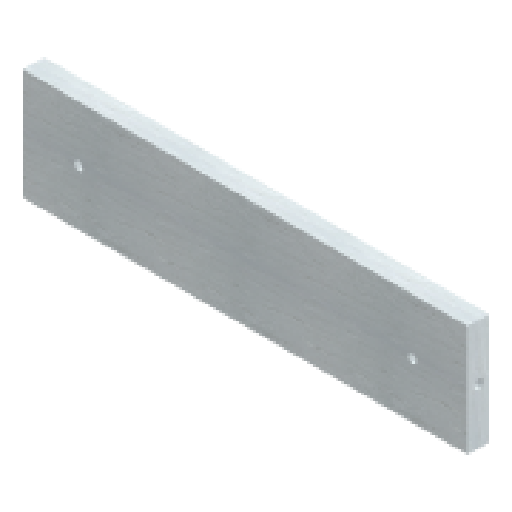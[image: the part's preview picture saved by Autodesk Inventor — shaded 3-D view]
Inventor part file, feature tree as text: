
AUTODESK INVENTOR PART (.ipt)
format: ipt  version: 2024 (Build 280153000, 153)  size: 125,440 bytes
history: native  units: in
note: dims shown in document units (in); Inventor stores cm internally (conversion verified against a paired STEP export)
features: extrude x4, sketch x4
ambient origin geometry x8: Origin, YZ Plane, XZ Plane, XY Plane, X Axis, Y Axis, Z Axis, Center Point
bodies: Solid1 (feature_tree)
feature tree (8):
  extrude  "Extrusion1"  Depth=3.937in
  extrude  "Extrusion2"  Depth=0.374in
  extrude  "Extrusion3"  Depth=0.315in
  extrude  "Extrusion4"  Depth=0.4331in TaperAngle=0.0deg
  sketch  "Sketch1"  dims[d0=15.748in d1=3.937in]
  sketch  "Sketch2"  dims[d2=0.374in d3=0.374in d4=0.0in d5=0.0in d6=1.9685in]
  sketch  "Sketch3"  dims[d7=1.9685in d8=0.315in]
  sketch  "Sketch4"  dims[d9=0.315in d10=0.4331in d11=0.0in d12=0.315in d13=0.4331in d14=0.0in d15=0.315in d16=0.4331in d17=0.0in]
